# Revit family: Roof-Ventilator_VEBK_Belt-Drive_Carnes
name_source: partatom
category: Mechanical Equipment
revit_build: Autodesk Revit Architecture 2012 (Build: 20110916_2132(x64)
units: mm (PartAtom-declared; Revit-internal decimal feet)

## types (13) — shared parameters
04 CSI = 23 34 23
95 CSI = 15830
Assembly Code = D3040200
Catalog URL = http://www.carnes.com
Default Elevation = 0"
Description = Centrifugal Roof Exhausters
Housing = Aluminum-Carnes-Spun-Brushed
IOM Instructions URL = http://www.carnes.com
Manufacturer = Carnes Company
Manufacturer Fax = 608-845-6470
Material = Spun Aluminum
Max. Motor Frame Size = 56
Model = VEBK
Parts List URL = http://www.carnes.com
Product Page URL = http://www.carnes.com
Specifications URL = http://www.carnes.com
Subcategory = Spun Aluminum Exhausters
URL = http://www.carnes.com
Warranty = http://www.carnes.com
Warranty URL = http://www.carnes.com
ecoScorecard Product Page = http://ecoscorecard.com

## per-type parameters (varying)
| type | Damper Size Sq. | E | Housing Radius | Inside Curb Cap | Roof Curb O.D. Sq. | Roof Opening Sq. | Tip Speed | Unit Diameter | Unit Height Extended | Unit Height Standard | Unit Weight (Less Motor) | Vent | Vent Radius | Vent/2 |
| VEBK06 | 10" | 2 7/8" | 12 7/8" | 15 1/2" | 14" | 11" | 2.75 x RPM | 25 3/4" | 26 5/8" | 21 7/8" | 30 Lbs. | 3 7/32" | 7 3/4" | 1 39/64" |
| VEBK08 | 10" | 4 1/4" | 12 7/8" | 15 1/2" | 14" | 11" | 2.75 x RPM | 25 3/4" | 28" | 23 1/4" | 30 Lbs. | 3 7/32" | 7 3/4" | 1 39/64" |
| VEBK10 | 12" | 3 1/2" | 13 7/8" | 17 5/8" | 16" | 13" | 3.27 x RPM | 27 3/4" | 28 5/8" | 23 7/8" | 35 Lbs. | 3 15/32" | 8 3/4" | 1 47/64" |
| VEBK12 | 12" | 5 1/8" | 13 7/8" | 17 5/8" | 16" | 13" | 3.27 x RPM | 27 3/4" | 30 1/4" | 25 1/2" | 35 Lbs. | 3 15/32" | 8 3/4" | 1 47/64" |
| VEBK15 | 15" | 6 1/2" | 16 3/8" | 20 1/2" | 19" | 16" | 4.06 x RPM | 32 3/4" | 33 1/4" | 28 1/2" | 50 Lbs. | 4 3/32" | 11 1/4" | 2 3/64" |
| VEBK18 | 19" | 7 3/4" | 18 7/8" | 25" | 23 1/2" | 20 1/2" | 4.94 x RPM | 37 3/4" | 34 3/8" | 29 5/8" | 65 Lbs. | 4 23/32" | 13 3/4" | 2 23/64" |
| VEBK21 | 22" | 8 3/4" | 21 3/8" | 28 1/8" | 26 1/2" | 23 1/2" | 5.76 x RPM | 42 3/4" | 38 1/8" | 34 1/8" | 100 Lbs. | 5 11/32" | 16 1/4" | 2 43/64" |
| VEBK24 | 26" | 9 3/4" | 23 3/8" | 31 1/8" | 29 1/2" | 26 1/2" | 6.68 x RPM | 46 3/4" | 41 3/8" | 37 3/8" | 125 Lbs. | 5 27/32" | 18 1/4" | 2 59/64" |
| VEBK30 | 34" | 10 7/8" | 27 7/8" | 40 1/8" | 38 1/2" | 35 1/2" | 8.25 x RPM | 55 3/4" | 49 1/8" | 42 3/8" | 190 Lbs. | 6 31/32" | 22 3/4" | 3 31/64" |
| VEBK36 | 40" | 12 3/4" | 32 3/8" | 46 1/8" | 44 1/2" | 41 1/2" | 9.62 x RPM | 64 3/4" | 52" | 45 1/4" | 310 Lbs. | 8 3/32" | 27 1/4" | 4 3/64" |
| VEBK42 | 48" | 14 1/4" | 36 3/8" | 54 1/8" | 52 1/2" | 49 1/2" | 11.26 x RPM | 72 3/4" | 55 3/4" | 49" | 490 Lbs. | 9 3/32" | 31 1/4" | 4 35/64" |
| VEBK48 | 52" | 15 1/8" | 40 3/8" | 58 1/8" | 56 1/2" | 53 1/2" | 12.83 x RPM | 80 3/4" | 58" | 51 1/4" | 540 Lbs. | 10 3/32" | 35 1/4" | 5 3/64" |
| VEBK54 | 58" | 24 1/8" | 44 3/8" | 64 1/8" | 62 1/2" | 59 1/2" | 14.40 x RPM | 88 3/4" | 63 5/8" | 56 5/8" | 665 Lbs. | 11 3/32" | 39 1/4" | 5 35/64" |

## geometry (parser evidence)
native form markers: Sweep x5
no freeform markers — native parametric forms only
